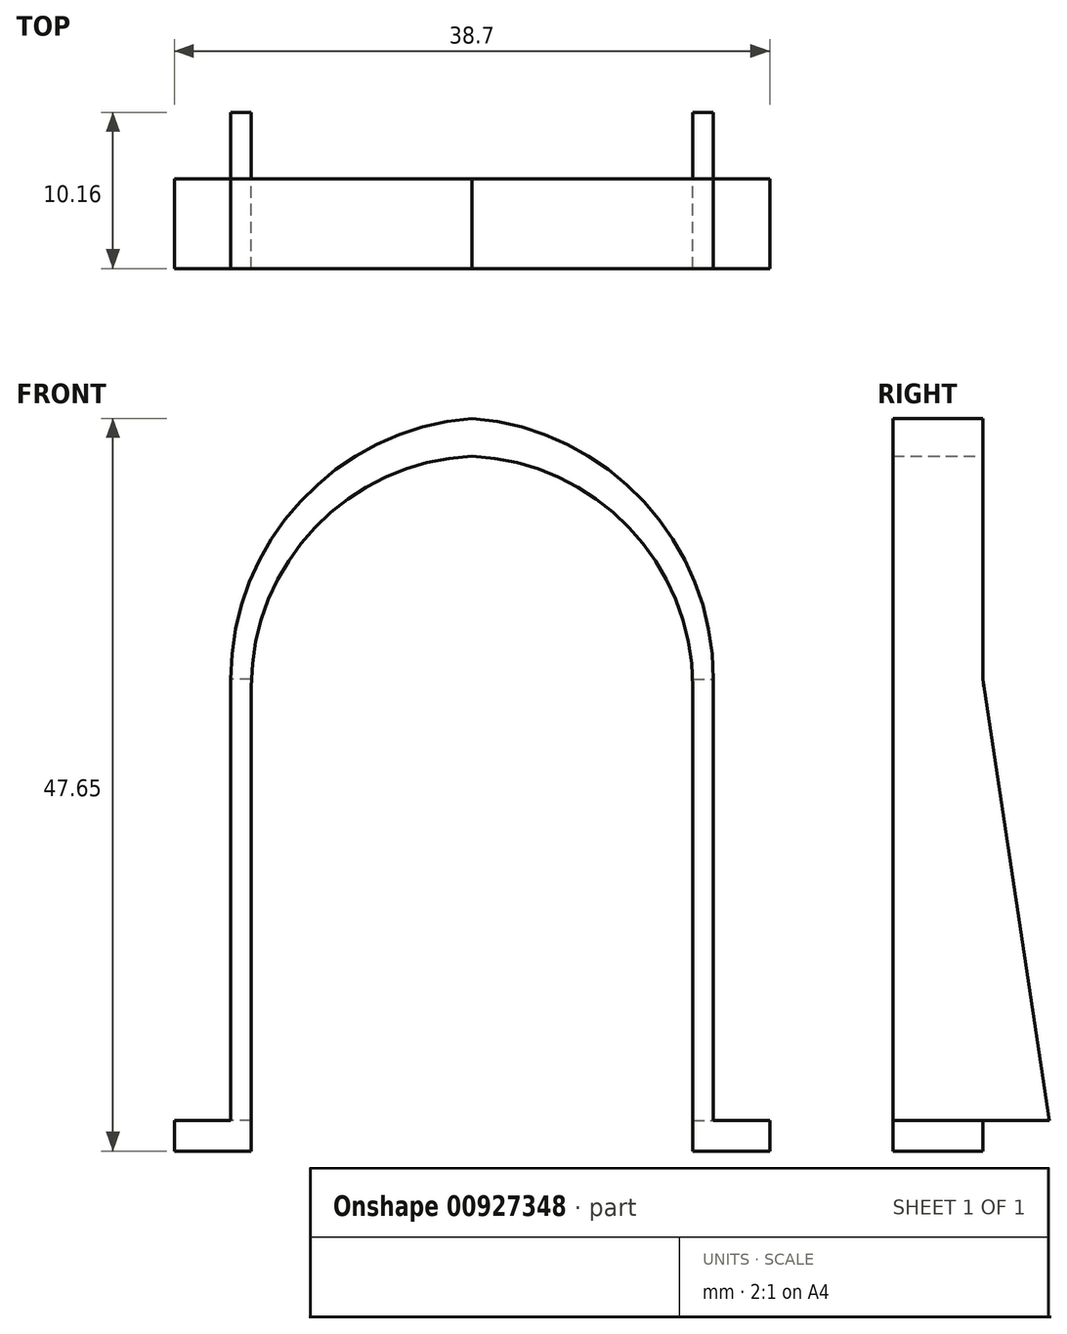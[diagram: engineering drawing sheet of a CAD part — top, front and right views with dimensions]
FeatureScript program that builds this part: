
annotation { "Feature Type Name" : "Feature", "Feature Type Description" : "" }
export const myFeature = defineFeature(function(context is Context, id is Id, definition is map)
    precondition{}
    {
        {
            var Q0;
            Q0=qCreatedBy(makeId("Front.planeOp"),FACE);
            var sketch = newSketch(context, id + "F0", { "sketchPlane" : qUnion([Q0])});
            skLineSegment(sketch, "E0.bottom", {"start": v(-14.35, 21.6) * mm, "end": v(14.35, 21.6) * mm});
            skLineSegment(sketch, "E0.top", {"start": v(-14.35, -21.6) * mm, "end": v(14.35, -21.6) * mm, "construction": true});
            skLineSegment(sketch, "E0.left", {"start": v(-14.35, 21.6) * mm, "end": v(-14.35, -21.6) * mm});
            skLineSegment(sketch, "E0.right", {"start": v(14.35, 21.6) * mm, "end": v(14.35, -21.6) * mm});
            skPoint(sketch, "E0.middle", {"position": v(0, 0) * mm});
            skLineSegment(sketch, "E1", {"start": v(-14.35, -21.6) * mm, "end": v(-15.68, -21.6) * mm});
            skLineSegment(sketch, "E2", {"start": v(-15.68, -21.6) * mm, "end": v(-15.68, 24.1) * mm});
            skLineSegment(sketch, "E3", {"start": v(-15.68, 24.1) * mm, "end": v(15.68, 24.1) * mm});
            skLineSegment(sketch, "E4", {"start": v(15.68, 24.1) * mm, "end": v(15.68, -21.6) * mm});
            skLineSegment(sketch, "E5", {"start": v(15.68, -21.6) * mm, "end": v(14.35, -21.6) * mm});
            skSolve(sketch);
        }
        {
            var Q0;
            Q0 = qSketchRegion(id + "F0", true);
            extrude(context, id + "F1", {"entities" : qUnion([Q0]), "endBound" : BoundingType.SYMMETRIC, "depth" : 5.84 * mm, "offsetDistance" : 25 * mm});
        }
        {
            var Q0;
            Q0=makeQuery(id+"F1.opExtrude","CAP_FACE",FACE,{"disambiguationData":[OSD([sQuery(id+"F0.wireOp",EDGE,"E0.bottom"),sQuery(id+"F0.wireOp",EDGE,"E0.left"),sQuery(id+"F0.wireOp",EDGE,"E0.right"),sQuery(id+"F0.wireOp",EDGE,"E1"),sQuery(id+"F0.wireOp",EDGE,"E2"),sQuery(id+"F0.wireOp",EDGE,"E3"),sQuery(id+"F0.wireOp",EDGE,"E4"),sQuery(id+"F0.wireOp",EDGE,"E5")])],"isStart":false});
            var sketch = newSketch(context, id + "F2", { "sketchPlane" : qUnion([Q0])});
            skLineSegment(sketch, "E6.0", {"start": v(-14.35, 21.6) * mm, "end": v(-14.35, -21.6) * mm});
            skLineSegment(sketch, "E7.0", {"start": v(14.35, 21.6) * mm, "end": v(14.35, -21.6) * mm});
            skLineSegment(sketch, "E8.bottom", {"start": v(-14.35, -21.6) * mm, "end": v(-19.35, -21.6) * mm});
            skLineSegment(sketch, "E8.top", {"start": v(-14.35, -23.6) * mm, "end": v(-19.35, -23.6) * mm});
            skLineSegment(sketch, "E8.left", {"start": v(-14.35, -21.6) * mm, "end": v(-14.35, -23.6) * mm});
            skLineSegment(sketch, "E8.right", {"start": v(-19.35, -21.6) * mm, "end": v(-19.35, -23.6) * mm});
            skLineSegment(sketch, "E9.bottom", {"start": v(14.35, -21.6) * mm, "end": v(19.35, -21.6) * mm});
            skLineSegment(sketch, "E9.top", {"start": v(14.35, -23.6) * mm, "end": v(19.35, -23.6) * mm});
            skLineSegment(sketch, "E9.left", {"start": v(14.35, -21.6) * mm, "end": v(14.35, -23.6) * mm});
            skLineSegment(sketch, "E9.right", {"start": v(19.35, -21.6) * mm, "end": v(19.35, -23.6) * mm});
            skSolve(sketch);
        }
        {
            var Q0;
            Q0=makeQuery(id+"F2.imprint","IMPRINT",FACE,{"disambiguationData":[TD([[makeQuery(id+"F2.imprint","IMPRINT",EDGE,{"derivedFrom":sQuery(id+"F2.wireOp",EDGE,"E8.top")}),-1.0]])]});
            var Q1;
            Q1=makeQuery(id+"F2.imprint","IMPRINT",FACE,{"disambiguationData":[TD([[makeQuery(id+"F2.imprint","IMPRINT",EDGE,{"derivedFrom":sQuery(id+"F2.wireOp",EDGE,"E9.top")}),1.0]])]});
            var Q2;
            Q2=makeQuery(id+"F1.opExtrude","CAP_FACE",FACE,{"disambiguationData":[OSD([sQuery(id+"F0.wireOp",EDGE,"E0.bottom"),sQuery(id+"F0.wireOp",EDGE,"E0.left"),sQuery(id+"F0.wireOp",EDGE,"E0.right"),sQuery(id+"F0.wireOp",EDGE,"E1"),sQuery(id+"F0.wireOp",EDGE,"E2"),sQuery(id+"F0.wireOp",EDGE,"E3"),sQuery(id+"F0.wireOp",EDGE,"E4"),sQuery(id+"F0.wireOp",EDGE,"E5")])],"isStart":true});
            extrude(context, id + "F3", {"entities" : qUnion([Q0, Q1]), "operationType" : NewBodyOperationType.ADD, "endBound" : BoundingType.UP_TO_SURFACE, "oppositeDirection" : true, "depth" : 25 * mm, "endBoundEntityFace" : qUnion([Q2]), "offsetDistance" : 25 * mm});
        }
        {
            var Q0;
            Q0=makeQuery(id+"F1.opExtrude","SWEPT_EDGE",EDGE,{"disambiguationData":[OSD([sQuery(id+"F0.wireOp",EDGE,"E0.bottom"),sQuery(id+"F0.wireOp",EDGE,"E0.left")])]});
            var Q1;
            Q1=makeQuery(id+"F1.opExtrude","SWEPT_EDGE",EDGE,{"disambiguationData":[OSD([sQuery(id+"F0.wireOp",EDGE,"E0.bottom"),sQuery(id+"F0.wireOp",EDGE,"E0.right")])]});
            fillet(context, id + "F4", {"entities" : qUnion([Q0, Q1]), "radius" : 15 * mm, "tangentPropagation" : true, "allowEdgeOverflow" : false});
        }
        {
            var Q0;
            Q0=makeQuery(id+"F1.opExtrude","SWEPT_EDGE",EDGE,{"disambiguationData":[OSD([sQuery(id+"F0.wireOp",EDGE,"E2"),sQuery(id+"F0.wireOp",EDGE,"E3")])]});
            var Q1;
            Q1=makeQuery(id+"F1.opExtrude","SWEPT_EDGE",EDGE,{"disambiguationData":[OSD([sQuery(id+"F0.wireOp",EDGE,"E3"),sQuery(id+"F0.wireOp",EDGE,"E4")])]});
            fillet(context, id + "F5", {"entities" : qUnion([Q0, Q1]), "radius" : 17 * mm, "tangentPropagation" : true, "allowEdgeOverflow" : false});
        }
        {
            var Q0;
            Q0=makeQuery(id+"F1.opExtrude","SWEPT_FACE",FACE,{"disambiguationData":[OSD([sQuery(id+"F0.wireOp",EDGE,"E2")])]});
            var sketch = newSketch(context, id + "F6", { "sketchPlane" : qUnion([Q0])});
            skLineSegment(sketch, "E10", {"start": v(-2.92, 7.1) * mm, "end": v(-7.24, -21.6) * mm});
            skLineSegment(sketch, "E11", {"start": v(-7.24, -21.6) * mm, "end": v(-2.92, -21.6) * mm});
            skSolve(sketch);
        }
        {
            var Q0;
            Q0=makeQuery(id+"F6.imprint","IMPRINT",FACE,{"disambiguationData":[TD([[makeQuery(id+"F6.imprint","IMPRINT",EDGE,{"derivedFrom":sQuery(id+"F6.wireOp",EDGE,"E10")}),1.0]])]});
            var Q1;
            Q1=makeQuery(id+"F3.boolean.opBoolean","MERGE",FACE,{"derivedFrom":[makeQuery(id+"F1.opExtrude","SWEPT_FACE",FACE,{"disambiguationData":[OSD([sQuery(id+"F0.wireOp",EDGE,"E0.left")])]}),makeQuery(id+"F3.opExtrude","SWEPT_FACE",FACE,{"disambiguationData":[OSD([sQuery(id+"F2.wireOp",EDGE,"E8.left")])]})]});
            extrude(context, id + "F7", {"entities" : qUnion([Q0]), "operationType" : NewBodyOperationType.ADD, "endBound" : BoundingType.UP_TO_SURFACE, "oppositeDirection" : true, "depth" : 25 * mm, "endBoundEntityFace" : qUnion([Q1]), "offsetDistance" : 25 * mm});
        }
        {
            var Q0;
            Q0=makeQuery(id+"F1.opExtrude","SWEPT_FACE",FACE,{"disambiguationData":[OSD([sQuery(id+"F0.wireOp",EDGE,"E4")])]});
            var sketch = newSketch(context, id + "F8", { "sketchPlane" : qUnion([Q0])});
            skLineSegment(sketch, "E12.0.0", {"start": v(2.92, -23.6) * mm, "end": v(2.92, -21.6) * mm});
            skLineSegment(sketch, "E12.0.1", {"start": v(2.92, -21.6) * mm, "end": v(7.24, -21.6) * mm});
            skLineSegment(sketch, "E12.0.2", {"start": v(7.24, -21.6) * mm, "end": v(2.92, 7.1) * mm});
            skLineSegment(sketch, "E12.0.3", {"start": v(2.92, 7.1) * mm, "end": v(2.92, 6.6) * mm});
            skLineSegment(sketch, "E12.0.4", {"start": v(2.92, 6.6) * mm, "end": v(-2.92, 6.6) * mm});
            skLineSegment(sketch, "E12.0.5", {"start": v(-2.92, 6.6) * mm, "end": v(-2.92, -23.6) * mm});
            skLineSegment(sketch, "E12.0.6", {"start": v(-2.92, -23.6) * mm, "end": v(2.92, -23.6) * mm});
            skSolve(sketch);
        }
        {
            var Q0;
            {var subQ0=sQuery(id+"F8.wireOp",EDGE,"E12.0.1");Q0=makeQuery(id+"F8.imprint","IMPRINT",FACE,{"disambiguationData":[TD([[makeQuery(id+"F8.imprint","IMPRINT",EDGE,{"derivedFrom":subQ0}),1.0]])]});}
            var Q1;
            Q1=makeQuery(id+"F3.boolean.opBoolean","MERGE",FACE,{"derivedFrom":[makeQuery(id+"F1.opExtrude","SWEPT_FACE",FACE,{"disambiguationData":[OSD([sQuery(id+"F0.wireOp",EDGE,"E0.right")])]}),makeQuery(id+"F3.opExtrude","SWEPT_FACE",FACE,{"disambiguationData":[OSD([sQuery(id+"F2.wireOp",EDGE,"E9.left")])]})]});
            extrude(context, id + "F9", {"entities" : qUnion([Q0]), "operationType" : NewBodyOperationType.ADD, "endBound" : BoundingType.UP_TO_SURFACE, "oppositeDirection" : true, "depth" : 25 * mm, "endBoundEntityFace" : qUnion([Q1]), "offsetDistance" : 25 * mm});
        }
    });
